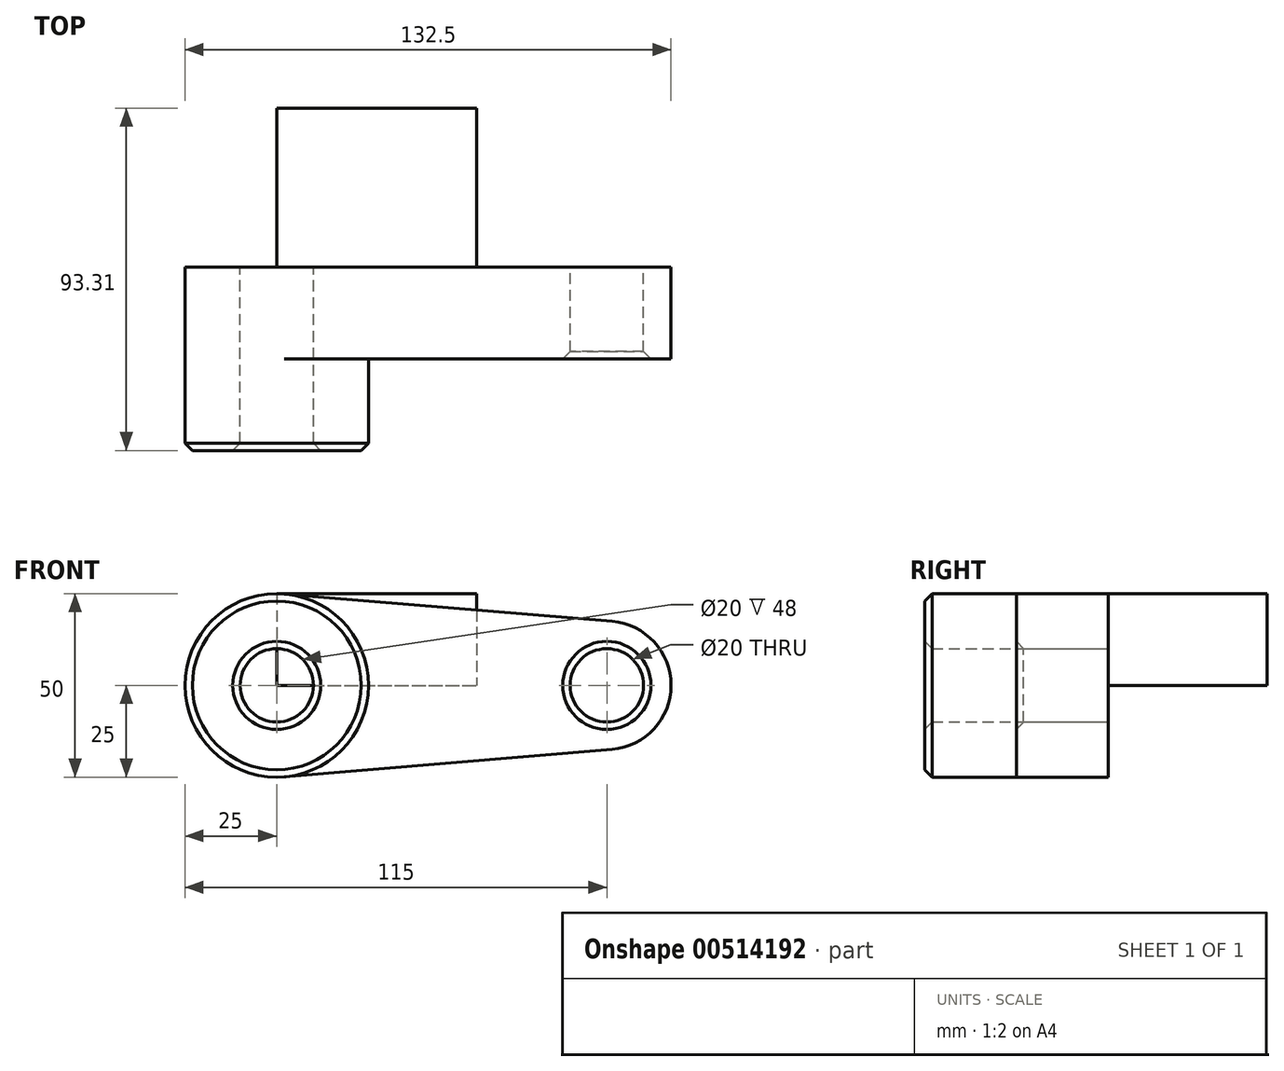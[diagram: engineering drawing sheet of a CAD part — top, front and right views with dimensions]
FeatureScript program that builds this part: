
annotation { "Feature Type Name" : "Feature", "Feature Type Description" : "" }
export const myFeature = defineFeature(function(context is Context, id is Id, definition is map)
    precondition{}
    {
        {
            var Q0;
            Q0=qCreatedBy(makeId("Front.planeOp"),FACE);
            var sketch = newSketch(context, id + "F0", { "sketchPlane" : qUnion([Q0])});
            skCircle(sketch, "E0", {"center": v(0, 0) * mm, "radius": 25 * mm});
            skCircle(sketch, "E1", {"center": v(90, 0) * mm, "radius": 17.5 * mm});
            skLineSegment(sketch, "E2", {"start": v(2.08, 24.91) * mm, "end": v(91.46, 17.44) * mm});
            skLineSegment(sketch, "E3", {"start": v(2.08, -24.91) * mm, "end": v(91.46, -17.44) * mm});
            skCircle(sketch, "E4", {"center": v(0, 0) * mm, "radius": 10 * mm});
            skCircle(sketch, "E5", {"center": v(90, 0) * mm, "radius": 10 * mm});
            skSolve(sketch);
        }
        {
            var Q0;
            Q0=qSketchRegion(id+"F0",true);
            extrude(context, id + "F1", {"entities" : qUnion([Q0]), "depth" : 25 * mm});
        }
        {
            var Q0;
            Q0=makeQuery(id+"F0.imprint","IMPRINT",FACE,{"disambiguationData":[TD([[makeQuery(id+"F0.imprint","IMPRINT",EDGE,{"derivedFrom":sQuery(id+"F0.wireOp",EDGE,"E4")}),-1.0]])]});
            extrude(context, id + "F2", {"entities" : qUnion([Q0]), "operationType" : NewBodyOperationType.ADD, "depth" : 50 * mm});
        }
        {
            var Q0;
            Q0=makeQuery(id+"F2.opExtrude","CAP_EDGE",EDGE,{"disambiguationData":[OSD([sQuery(id+"F0.wireOp",EDGE,"E0")])],"isStart":false});
            var Q1;
            Q1=makeQuery(id+"F2.opExtrude","CAP_EDGE",EDGE,{"disambiguationData":[OSD([sQuery(id+"F0.wireOp",EDGE,"E4")])],"isStart":false});
            var Q2;
            Q2=makeQuery(id+"F1.opExtrude","CAP_EDGE",EDGE,{"disambiguationData":[OSD([sQuery(id+"F0.wireOp",EDGE,"E5")])],"isStart":false});
            chamfer(context, id + "F3", {"entities" : qUnion([Q0, Q1, Q2]), "width" : 2 * mm, "tangentPropagation" : true});
        }
        {
            var Q0;
            Q0=qCreatedBy(makeId("Top.planeOp"),FACE);
            var sketch = newSketch(context, id + "F4", { "sketchPlane" : qUnion([Q0])});
            skLineSegment(sketch, "E6.bottom", {"start": v(0, 0) * mm, "end": v(54.48, 0) * mm});
            skLineSegment(sketch, "E6.top", {"start": v(0, 43.31) * mm, "end": v(54.48, 43.31) * mm});
            skLineSegment(sketch, "E6.left", {"start": v(0, 0) * mm, "end": v(0, 43.31) * mm});
            skLineSegment(sketch, "E6.right", {"start": v(54.48, 0) * mm, "end": v(54.48, 43.31) * mm});
            skSolve(sketch);
        }
        {
            var Q0;
            Q0 = qSketchRegion(id + "F4", true);
            extrude(context, id + "F5", {"entities" : qUnion([Q0]), "operationType" : NewBodyOperationType.ADD, "depth" : 25 * mm});
        }
    });
